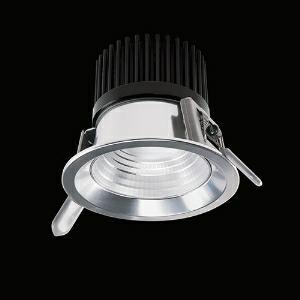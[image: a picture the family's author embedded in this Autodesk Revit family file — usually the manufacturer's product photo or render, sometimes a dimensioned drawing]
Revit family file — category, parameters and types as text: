
# Revit family: spectral_myral_myral_3500-830-m-dali
name_source: partatom
category: Lighting Fixtures
revit_build: Autodesk Revit 2016 (Build: 20150220_1215(x64)
units: mm (PartAtom-declared; Revit-internal decimal feet)

## family parameters
Cut with Voids When Loaded = No
Host = Face
Light Source = No
Part Type = Normal
Room Calculation Point = No
Round Connector Dimension = Use Diameter
Shared = No

## types (1)
- SPECTRAL MYRAL (1 x )
    Apparent Load = 0 VA
    Approval mark = CE
    CIE Flux Codes = 82 99 100 100 100
    Control Gear = Electronic transformer
    Default Elevation = 1800 mm
    Description = SPG0330180
MYRAL recessed spot

Design:
    Height = 0 mm  [stored 0 ft]
    Lamp = 1 x
    Lamp count = 1
    Length = 120 mm
    Luminous efficacy = 0 lm/W
    Manufacturer = Ridi
    ModVariant = No
    Model = MYRAL 3500-830-M-DALI
    Mounting Place = Ceiling
    Mounting Type = Recessed
    Number of Poles = 1
    OnlyDefault = Yes
    Power Factor = 1
    Product Name = SPECTRAL MYRAL
    Product group = Downlight recessed
    ProductGroupID = 400
    Protection Class = Protection class
    Protection Degree = IP 20
    RlxData = <blob elided: 38681 chars, md5=99df96ee>
    Socket = socket
    Standby Power = 0 W
    System Light Flux = 0 lm
    System Power = 0 W
    Type Image = myral_04.jpg
    URL = http://reluxnet.relux.com
    VarID = ---
    Voltage = 0 V
    Weight = 0.00 kg
    Width = 0 mm  [stored 0 ft]

note: [stored X ft] marks values corroborated as IEEE doubles in the binary element streams (Revit-internal decimal feet)

## geometry (parser evidence)
native form markers: Sweep x11
no freeform markers — native parametric forms only
